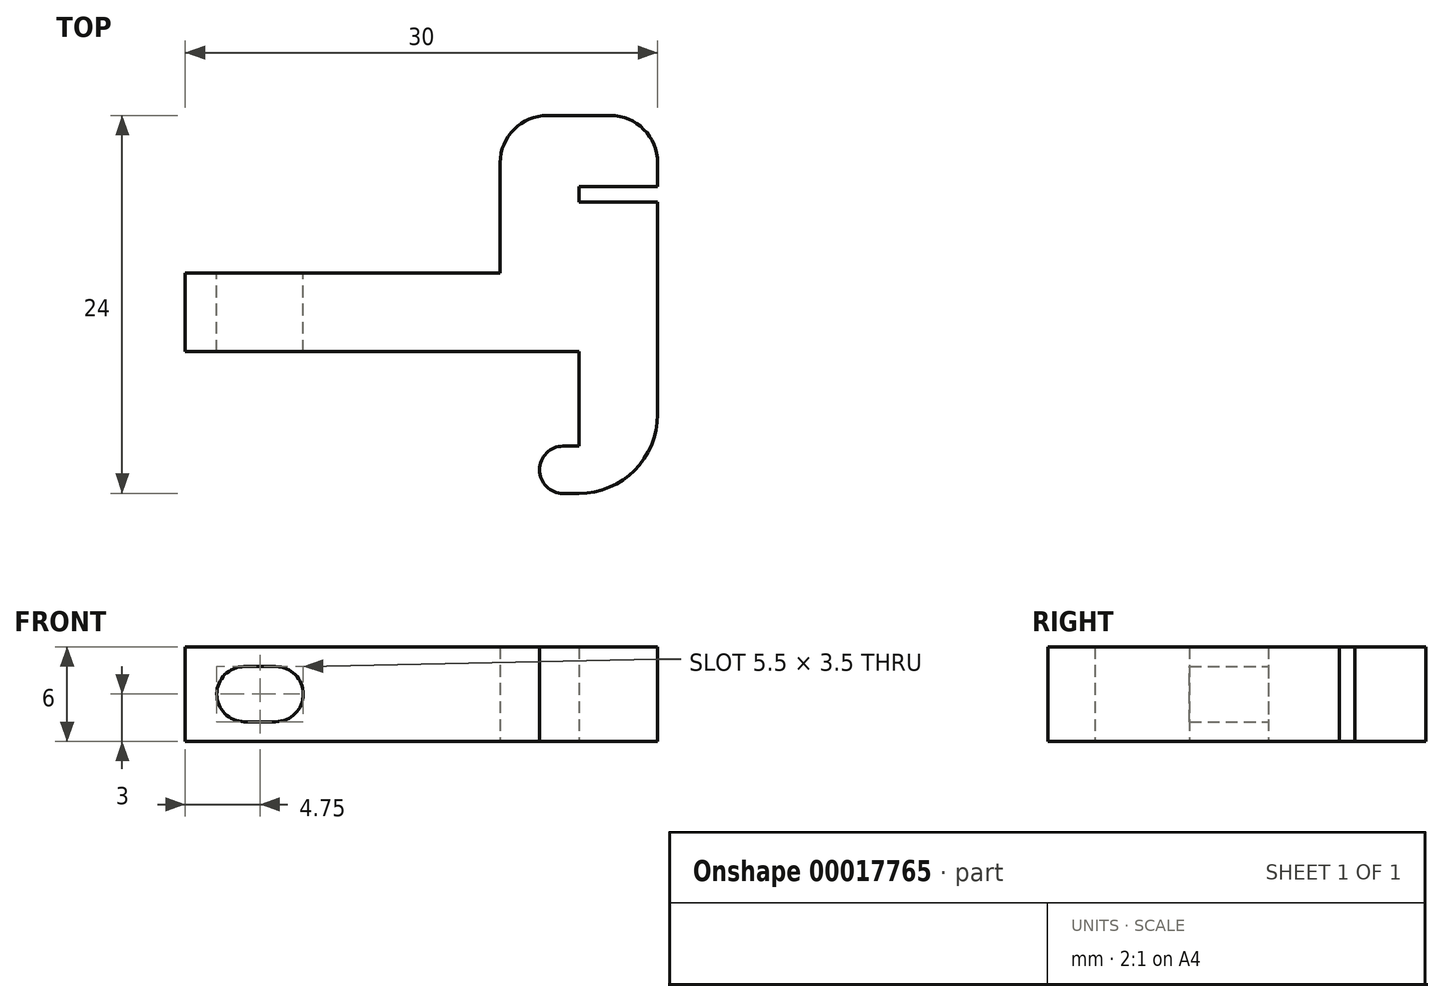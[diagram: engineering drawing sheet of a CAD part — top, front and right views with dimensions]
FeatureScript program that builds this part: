
annotation { "Feature Type Name" : "Feature", "Feature Type Description" : "" }
export const myFeature = defineFeature(function(context is Context, id is Id, definition is map)
    precondition{}
    {
        {
            var Q0;
            Q0=qCreatedBy(makeId("Top.planeOp"),FACE);
            var sketch = newSketch(context, id + "F0", { "sketchPlane" : qUnion([Q0])});
            skLineSegment(sketch, "E0", {"start": v(0, 0) * mm, "end": v(5, 0) * mm});
            skLineSegment(sketch, "E1", {"start": v(5, 0) * mm, "end": v(5, 14) * mm});
            skLineSegment(sketch, "E2", {"start": v(5, 14) * mm, "end": v(-25, 14) * mm});
            skLineSegment(sketch, "E3", {"start": v(-25, 14) * mm, "end": v(-25, 9) * mm});
            skLineSegment(sketch, "E4", {"start": v(-25, 9) * mm, "end": v(0, 9) * mm});
            skLineSegment(sketch, "E5", {"start": v(0, 9) * mm, "end": v(0, 3) * mm});
            skLineSegment(sketch, "E6", {"start": v(0, 3) * mm, "end": v(-1, 3) * mm});
            skLineSegment(sketch, "E7", {"start": v(0, 0) * mm, "end": v(-1, 0) * mm});
            skArc(sketch, "E8", {"start": v(-1, 3) * mm, "mid": v(-2.5, 1.5) * mm, "end": v(-1, 0) * mm});
            skSolve(sketch);
        }
        {
            var Q0;
            Q0=qSketchRegion(id+"F0",true);
            extrude(context, id + "F1", {"entities" : qUnion([Q0]), "depth" : 6 * mm});
        }
        {
            var Q0;
            Q0=makeQuery(id+"F1.opExtrude","SWEPT_FACE",FACE,{"disambiguationData":[OSD([sQuery(id+"F0.wireOp",EDGE,"E2")])]});
            var sketch = newSketch(context, id + "F2", { "sketchPlane" : qUnion([Q0])});
            skCircle(sketch, "E9", {"center": v(21.25, 3) * mm, "radius": 1.75 * mm});
            skLineSegment(sketch, "E10", {"start": v(21.25, 6) * mm, "end": v(21.25, 0) * mm});
            skCircle(sketch, "E11", {"center": v(19.25, 3) * mm, "radius": 1.75 * mm});
            skLineSegment(sketch, "E12", {"start": v(19.25, 4.75) * mm, "end": v(21.25, 4.75) * mm});
            skLineSegment(sketch, "E13", {"start": v(19.25, 1.25) * mm, "end": v(21.25, 1.25) * mm});
            skSolve(sketch);
        }
        {
            var Q0;
            Q0=qSketchRegion(id+"F2",true);
            var Q1;
            {var subQ0=sQuery(id+"F2.wireOp",EDGE,"E11");var subQ1=sQuery(id+"F2.wireOp",EDGE,"E9");var subQ3=makeQuery(id+"F2.imprint","INTERSECT",VERTEX,{"disambiguationData":[OD(0.0)],"derivedFrom":[subQ1,subQ0]});Q1=makeQuery(id+"F2.imprint","IMPRINT",FACE,{"disambiguationData":[TD([[makeQuery(id+"F2.imprint","IMPRINT",EDGE,{"disambiguationData":[TD([[subQ3,-1.0]])],"derivedFrom":subQ1}),1.0]])]});}
            extrude(context, id + "F3", {"entities" : qUnion([Q0, Q1]), "operationType" : NewBodyOperationType.REMOVE, "oppositeDirection" : true, "depth" : 25 * mm, "hasSecondDirection" : true, "secondDirectionOppositeDirection" : false, "secondDirectionDepth" : 25 * mm});
        }
        {
            var Q0;
            Q0=makeQuery(id+"F1.opExtrude","SWEPT_FACE",FACE,{"disambiguationData":[OSD([sQuery(id+"F0.wireOp",EDGE,"E2")])]});
            var sketch = newSketch(context, id + "F4", { "sketchPlane" : qUnion([Q0])});
            skLineSegment(sketch, "E14.bottom", {"start": v(-5, 6) * mm, "end": v(5, 6) * mm});
            skLineSegment(sketch, "E14.top", {"start": v(-5, 0) * mm, "end": v(5, 0) * mm});
            skLineSegment(sketch, "E14.left", {"start": v(-5, 6) * mm, "end": v(-5, 0) * mm});
            skLineSegment(sketch, "E14.right", {"start": v(5, 6) * mm, "end": v(5, 0) * mm});
            skLineSegment(sketch, "E15", {"start": v(10.64, 6) * mm, "end": v(5, 6) * mm, "construction": true});
            skLineSegment(sketch, "E16.0", {"start": v(-3, 17.37) * mm, "end": v(-3, -11.33) * mm, "construction": true});
            skSolve(sketch);
        }
        {
            var Q0;
            Q0=qSketchRegion(id+"F4",true);
            extrude(context, id + "F5", {"entities" : qUnion([Q0]), "operationType" : NewBodyOperationType.ADD, "depth" : 10 * mm});
        }
        {
            var Q0;
            Q0=makeQuery(id+"F5.opExtrude","CAP_EDGE",EDGE,{"disambiguationData":[OSD([sQuery(id+"F4.wireOp",EDGE,"E14.left")])],"isStart":false});
            var Q1;
            Q1=makeQuery(id+"F5.opExtrude","CAP_EDGE",EDGE,{"disambiguationData":[OSD([sQuery(id+"F4.wireOp",EDGE,"E14.right")])],"isStart":false});
            fillet(context, id + "F6", {"entities" : qUnion([Q0, Q1]), "radius" : 3 * mm, "tangentPropagation" : true, "allowEdgeOverflow" : false});
        }
        {
            var Q0;
            Q0=makeQuery(id+"F1.opExtrude","SWEPT_EDGE",EDGE,{"disambiguationData":[OSD([sQuery(id+"F0.wireOp",EDGE,"E0"),sQuery(id+"F0.wireOp",EDGE,"E1")])]});
            fillet(context, id + "F7", {"entities" : qUnion([Q0]), "radius" : 5 * mm, "tangentPropagation" : true, "allowEdgeOverflow" : false});
        }
        {
            var Q0;
            Q0=makeQuery(id+"F5.boolean.opBoolean","MERGE",FACE,{"derivedFrom":[makeQuery(id+"F1.opExtrude","CAP_FACE",FACE,{"disambiguationData":[OSD([sQuery(id+"F0.wireOp",EDGE,"E0"),sQuery(id+"F0.wireOp",EDGE,"E1"),sQuery(id+"F0.wireOp",EDGE,"E2"),sQuery(id+"F0.wireOp",EDGE,"E3"),sQuery(id+"F0.wireOp",EDGE,"E4"),sQuery(id+"F0.wireOp",EDGE,"E5"),sQuery(id+"F0.wireOp",EDGE,"E6"),sQuery(id+"F0.wireOp",EDGE,"E7"),sQuery(id+"F0.wireOp",EDGE,"E8")])],"isStart":true}),makeQuery(id+"F5.opExtrude","SWEPT_FACE",FACE,{"disambiguationData":[OSD([sQuery(id+"F4.wireOp",EDGE,"E14.top")])]})]});
            var sketch = newSketch(context, id + "F8", { "sketchPlane" : qUnion([Q0])});
            skLineSegment(sketch, "E17.0", {"start": v(20.04, -19) * mm, "end": v(-25, -19) * mm, "construction": true});
            skLineSegment(sketch, "E18.0", {"start": v(20.04, -18.5) * mm, "end": v(0, -18.5) * mm});
            skLineSegment(sketch, "E19.0", {"start": v(20.04, -19.5) * mm, "end": v(0, -19.5) * mm});
            skLineSegment(sketch, "E20.0", {"start": v(0, -5) * mm, "end": v(0, -22.15) * mm, "construction": true});
            skLineSegment(sketch, "E21", {"start": v(0, -19.5) * mm, "end": v(0, -18.5) * mm});
            skLineSegment(sketch, "E22", {"start": v(20.04, -19.5) * mm, "end": v(20.04, -18.5) * mm});
            skSolve(sketch);
        }
        {
            var Q0;
            Q0 = qSketchRegion(id + "F8", true);
            extrude(context, id + "F9", {"entities" : qUnion([Q0]), "operationType" : NewBodyOperationType.REMOVE, "oppositeDirection" : true, "depth" : 25 * mm});
        }
    });
